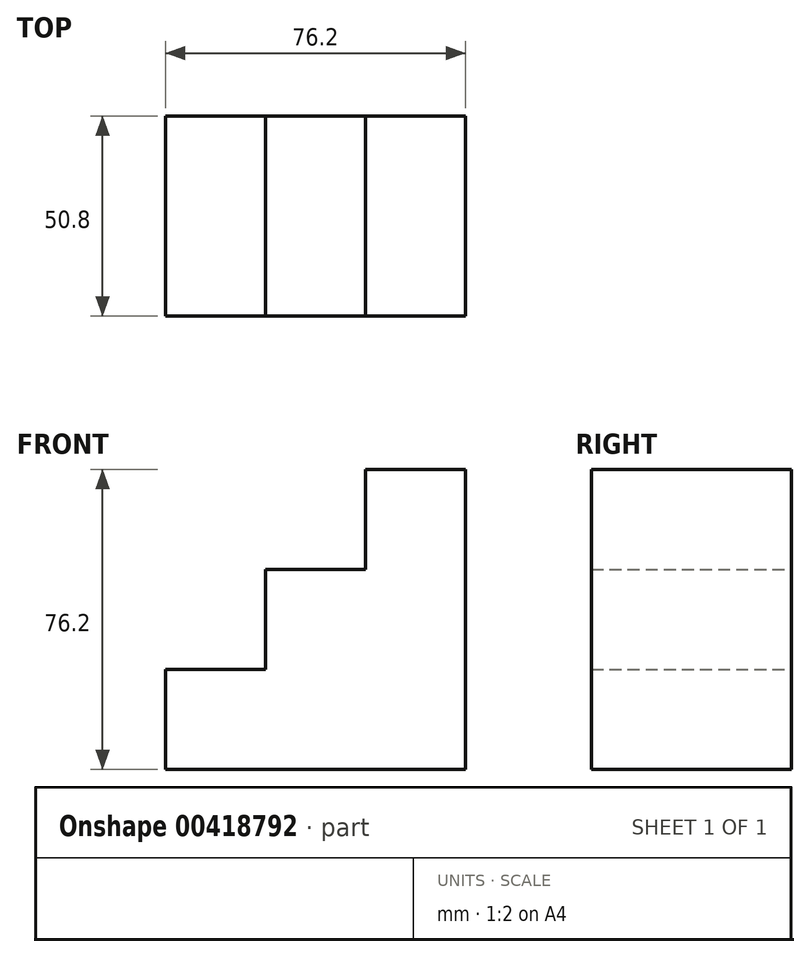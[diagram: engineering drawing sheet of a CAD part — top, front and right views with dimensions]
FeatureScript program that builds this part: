
annotation { "Feature Type Name" : "Feature", "Feature Type Description" : "" }
export const myFeature = defineFeature(function(context is Context, id is Id, definition is map)
    precondition{}
    {
        {
            var Q0;
            Q0=qCreatedBy(makeId("Front.planeOp"),FACE);
            var sketch = newSketch(context, id + "F0", { "sketchPlane" : qUnion([Q0])});
            skLineSegment(sketch, "E0", {"start": v(0, 0) * mm, "end": v(76.2, 0) * mm});
            skLineSegment(sketch, "E1", {"start": v(76.2, 0) * mm, "end": v(76.2, 76.2) * mm});
            skLineSegment(sketch, "E2", {"start": v(76.2, 76.2) * mm, "end": v(50.8, 76.2) * mm});
            skLineSegment(sketch, "E3", {"start": v(50.8, 76.2) * mm, "end": v(50.8, 50.8) * mm});
            skLineSegment(sketch, "E4", {"start": v(50.8, 50.8) * mm, "end": v(25.4, 50.8) * mm});
            skLineSegment(sketch, "E5", {"start": v(25.4, 50.8) * mm, "end": v(25.4, 25.4) * mm});
            skLineSegment(sketch, "E6", {"start": v(25.4, 25.4) * mm, "end": v(0, 25.4) * mm});
            skLineSegment(sketch, "E7", {"start": v(0, 25.4) * mm, "end": v(0, 0) * mm});
            skSolve(sketch);
        }
        {
            var Q0;
            Q0=makeQuery(id+"F0.imprint","IMPRINT",FACE,{"disambiguationData":[TD([[makeQuery(id+"F0.imprint","IMPRINT",EDGE,{"derivedFrom":sQuery(id+"F0.wireOp",EDGE,"E0")}),1.0]])]});
            extrude(context, id + "F1", {"entities" : qUnion([Q0]), "depth" : 50.8 * mm});
        }
    });
